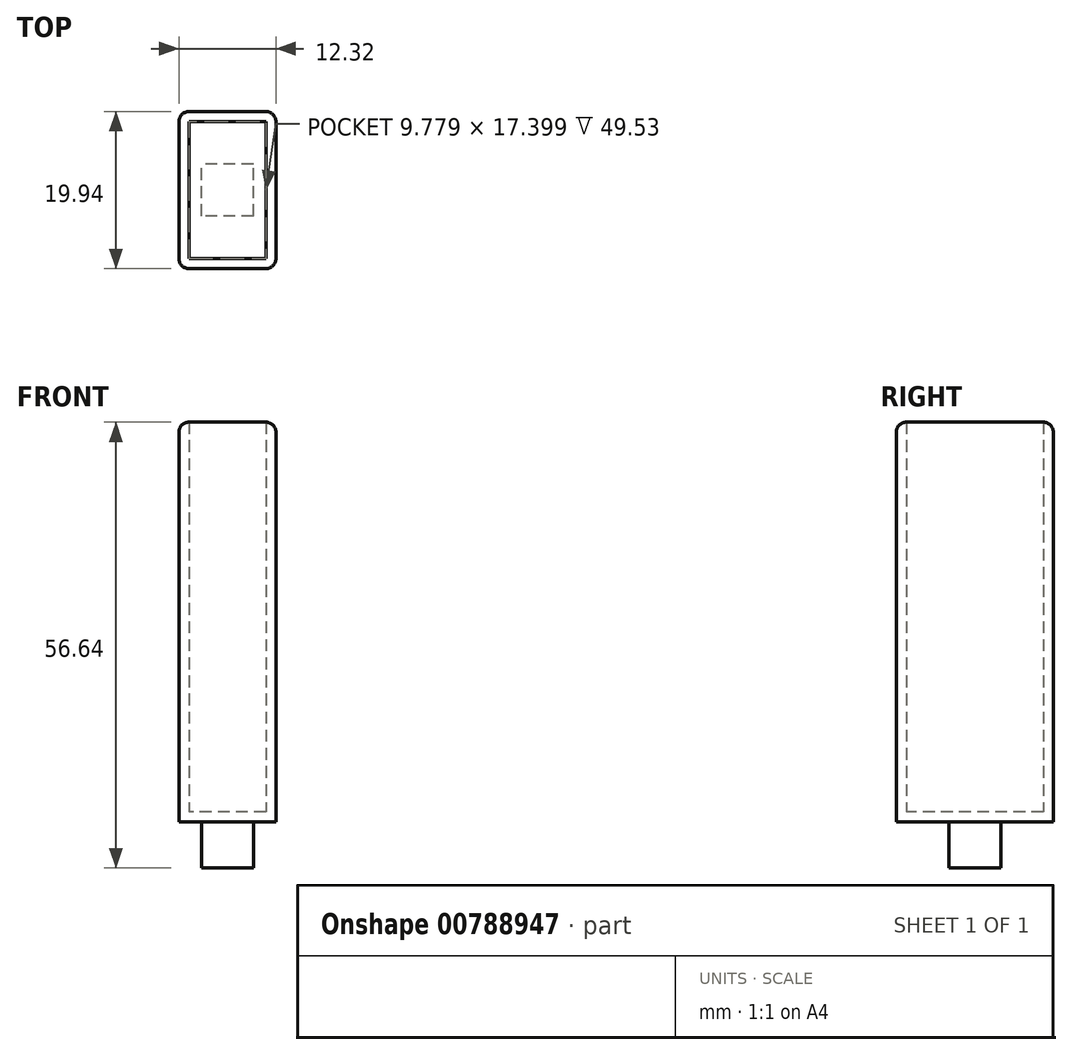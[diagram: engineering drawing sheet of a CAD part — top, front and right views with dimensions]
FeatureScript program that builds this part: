
annotation { "Feature Type Name" : "Feature", "Feature Type Description" : "" }
export const myFeature = defineFeature(function(context is Context, id is Id, definition is map)
    precondition{}
    {
        {
            var Q0;
            Q0=qCreatedBy(makeId("Top.planeOp"),FACE);
            var sketch = newSketch(context, id + "F0", { "sketchPlane" : qUnion([Q0])});
            skLineSegment(sketch, "E0.bottom", {"start": v(6.16, 9.97) * mm, "end": v(-6.16, 9.97) * mm});
            skLineSegment(sketch, "E0.top", {"start": v(6.16, -9.97) * mm, "end": v(-6.16, -9.97) * mm});
            skLineSegment(sketch, "E0.left", {"start": v(6.16, 9.97) * mm, "end": v(6.16, -9.97) * mm});
            skLineSegment(sketch, "E0.right", {"start": v(-6.16, 9.97) * mm, "end": v(-6.16, -9.97) * mm});
            skPoint(sketch, "E0.middle", {"position": v(0, 0) * mm});
            skSolve(sketch);
        }
        {
            var Q0;
            Q0=makeQuery(id+"F0.imprint","IMPRINT",FACE,{"disambiguationData":[TD([[makeQuery(id+"F0.imprint","IMPRINT",EDGE,{"derivedFrom":sQuery(id+"F0.wireOp",EDGE,"E0.bottom")}),1.0]])]});
            extrude(context, id + "F1", {"entities" : qUnion([Q0]), "depth" : 50.8 * mm, "offsetDistance" : 25.4 * mm});
        }
        {
            var Q0;
            Q0=makeQuery(id+"F1.opExtrude","CAP_FACE",FACE,{"disambiguationData":[OSD([sQuery(id+"F0.wireOp",EDGE,"E0.bottom"),sQuery(id+"F0.wireOp",EDGE,"E0.top"),sQuery(id+"F0.wireOp",EDGE,"E0.left"),sQuery(id+"F0.wireOp",EDGE,"E0.right")])],"isStart":false});
            shell(context, id + "F2", {"entities" : qUnion([Q0]), "thickness" : 1.27 * mm});
        }
        {
            var Q0;
            Q0=makeQuery(id+"F1.opExtrude","CAP_EDGE",EDGE,{"disambiguationData":[OSD([sQuery(id+"F0.wireOp",EDGE,"E0.top")])],"isStart":false});
            var Q1;
            Q1=makeQuery(id+"F1.opExtrude","CAP_EDGE",EDGE,{"disambiguationData":[OSD([sQuery(id+"F0.wireOp",EDGE,"E0.left")])],"isStart":false});
            var Q2;
            Q2=makeQuery(id+"F1.opExtrude","CAP_EDGE",EDGE,{"disambiguationData":[OSD([sQuery(id+"F0.wireOp",EDGE,"E0.bottom")])],"isStart":false});
            var Q3;
            Q3=makeQuery(id+"F1.opExtrude","CAP_EDGE",EDGE,{"disambiguationData":[OSD([sQuery(id+"F0.wireOp",EDGE,"E0.right")])],"isStart":false});
            var Q4;
            Q4=makeQuery(id+"F1.opExtrude","SWEPT_EDGE",EDGE,{"disambiguationData":[OSD([sQuery(id+"F0.wireOp",EDGE,"E0.top"),sQuery(id+"F0.wireOp",EDGE,"E0.right")])]});
            var Q5;
            Q5=makeQuery(id+"F1.opExtrude","SWEPT_EDGE",EDGE,{"disambiguationData":[OSD([sQuery(id+"F0.wireOp",EDGE,"E0.top"),sQuery(id+"F0.wireOp",EDGE,"E0.left")])]});
            var Q6;
            Q6=makeQuery(id+"F1.opExtrude","SWEPT_EDGE",EDGE,{"disambiguationData":[OSD([sQuery(id+"F0.wireOp",EDGE,"E0.bottom"),sQuery(id+"F0.wireOp",EDGE,"E0.left")])]});
            var Q7;
            Q7=makeQuery(id+"F1.opExtrude","SWEPT_EDGE",EDGE,{"disambiguationData":[OSD([sQuery(id+"F0.wireOp",EDGE,"E0.bottom"),sQuery(id+"F0.wireOp",EDGE,"E0.right")])]});
            fillet(context, id + "F3", {"entities" : qUnion([Q0, Q1, Q2, Q3, Q4, Q5, Q6, Q7]), "radius" : 1.27 * mm, "tangentPropagation" : true, "allowEdgeOverflow" : false});
        }
        {
            var Q0;
            Q0=makeQuery(id+"F1.opExtrude","CAP_FACE",FACE,{"disambiguationData":[OSD([sQuery(id+"F0.wireOp",EDGE,"E0.bottom"),sQuery(id+"F0.wireOp",EDGE,"E0.top"),sQuery(id+"F0.wireOp",EDGE,"E0.left"),sQuery(id+"F0.wireOp",EDGE,"E0.right")])],"isStart":true});
            var sketch = newSketch(context, id + "F4", { "sketchPlane" : qUnion([Q0])});
            skLineSegment(sketch, "E1.bottom", {"start": v(3.3, 3.3) * mm, "end": v(-3.3, 3.3) * mm});
            skLineSegment(sketch, "E1.top", {"start": v(3.3, -3.3) * mm, "end": v(-3.3, -3.3) * mm});
            skLineSegment(sketch, "E1.left", {"start": v(3.3, 3.3) * mm, "end": v(3.3, -3.3) * mm});
            skLineSegment(sketch, "E1.right", {"start": v(-3.3, 3.3) * mm, "end": v(-3.3, -3.3) * mm});
            skPoint(sketch, "E1.middle", {"position": v(0, 0) * mm});
            skSolve(sketch);
        }
        {
            var Q0;
            Q0=makeQuery(id+"F4.imprint","IMPRINT",FACE,{"disambiguationData":[TD([[makeQuery(id+"F4.imprint","IMPRINT",EDGE,{"derivedFrom":sQuery(id+"F4.wireOp",EDGE,"E1.bottom")}),1.0]])]});
            extrude(context, id + "F5", {"entities" : qUnion([Q0]), "operationType" : NewBodyOperationType.ADD, "depth" : 5.84 * mm, "offsetDistance" : 25.4 * mm});
        }
    });
